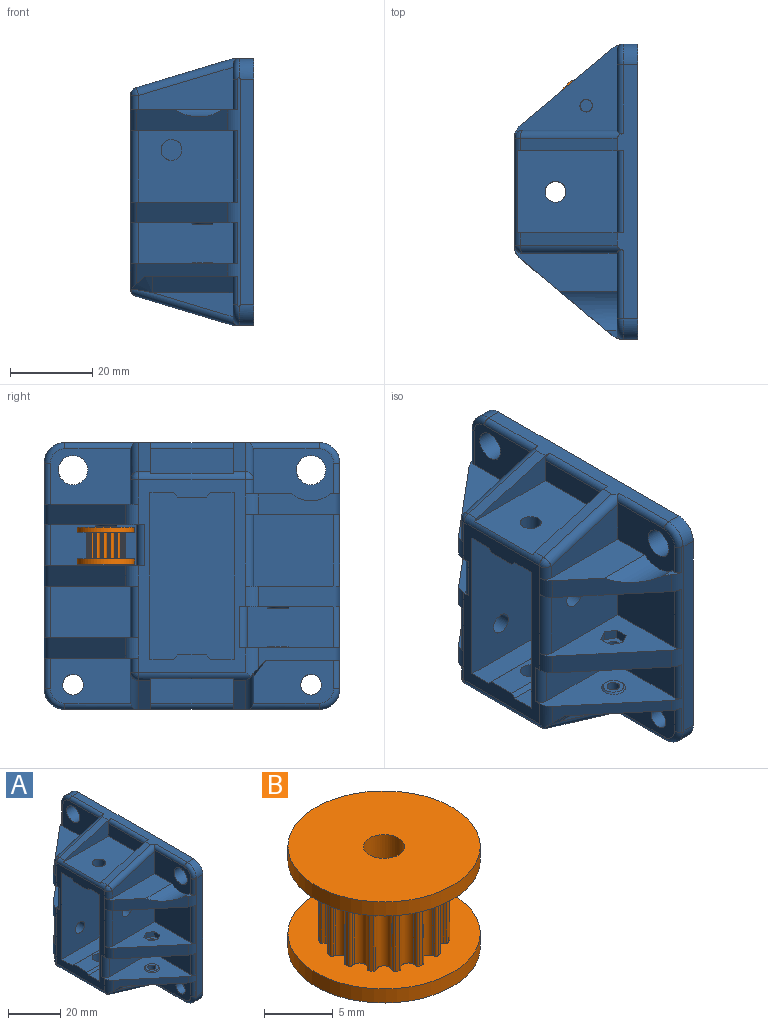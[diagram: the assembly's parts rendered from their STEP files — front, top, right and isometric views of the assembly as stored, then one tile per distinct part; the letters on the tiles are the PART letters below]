
ASSEMBLY  parts=2 mates=1
PART A: 149 faces, bbox 30.9x73.2x66.2 mm
  f0: cylinder r=1.55mm len=3.1mm, axis (0,0,1), area 30.2mm2, adj f78,f124
  f1: cylinder r=1.55mm len=3.1mm, axis (0,0,-1), area 30.2mm2, adj f81,f117
  f2: plane 3.79x2.2mm, normal (0,0,1), area 3.1mm2, adj f7,f71,f90,f108,f115
  f3: plane 25x11.25mm, normal (0,0,1), area 180.6mm2, adj f7,f19,f37,f71,f90,f132,f148
  f4: plane 20x6mm, normal (-1,0,0), area 120mm2, adj f5,f64,f65,f109
  f5: plane 24.34x20mm, normal (0,0,-1), area 466.3mm2, adj f4,f64,f65,f86,f136
  f6: plane 19.58x11mm, normal (-1,0,0), area 192.1mm2, adj f28,f41,f56,f94,f103,f104,f105
  f7: plane 19.58x12.7mm, normal (-1,0,0), area 183mm2, adj f2,f3,f26,f37,f90,f91,f106,f107
  f8: plane 24.34x20mm, normal (0,0,1), area 466.3mm2, adj f9,f62,f63,f87,f135
  f9: plane 20x6mm, normal (-1,0,0), area 120mm2, adj f8,f62,f63,f110
  f10: plane 21x10mm, normal (-1,0,0), area 210mm2, adj f34,f35,f36,f111
  f11: plane 21x10mm, normal (-1,0,0), area 210mm2, adj f38,f39,f40,f114
  f12: plane 19.5x17.5mm, normal (-1,0,0), area 341.3mm2, adj f13,f59,f61,f113
  f13: plane 23x17.5mm, normal (0,-1,0), area 382.1mm2, adj f12,f59,f61,f88,f139
  f14: plane 19.58x10.5mm, normal (-1,0,0), area 176.3mm2, adj f15,f29,f58,f93,f95,f100,f101,f102
  f15: plane 19.71x5.91mm, normal (0,-1,0), area 58.3mm2, adj f14,f93,f95
  f16: plane 19.58x13.5mm, normal (-1,0,0), area 220.7mm2, adj f18,f27,f55,f92,f97,f98,f99
  f17: plane 23x12.5mm, normal (0,1,0), area 267.1mm2, adj f20,f57,f60,f89,f140
  f18: plane 23x12.91mm, normal (0,1,0), area 217.6mm2, adj f16,f55,f92,f131
  f19: plane 47.02x26.27mm, normal (-1,0,0), area 382.6mm2, adj f3,f34,f36,f38,f40,f42,f43,f44
  f20: plane 19.5x12.5mm, normal (-1,0,0), area 243.8mm2, adj f17,f57,f60,f112
  f21: plane 55x3.18mm, normal (0,-1,0), area 174.8mm2, adj f25,f30,f33,f115
  f22: plane 62x5mm, normal (0,0,-1), area 228.5mm2, adj f25,f30,f31,f64,f65,f72,f73,f93
  f23: plane 55x3.18mm, normal (0,1,0), area 174.8mm2, adj f25,f31,f32,f116
  f24: plane 62x5mm, normal (0,0,1), area 228.5mm2, adj f25,f32,f33,f62,f63,f74,f75,f91
  f25: plane 72x65mm, normal (1,0,0), area 4539.1mm2, adj f21,f22,f23,f24,f26,f27,f28,f29
  f26: cylinder r=3.56mm len=7.13mm, axis (1,0,0), area 112mm2, adj f7,f25
  f27: cylinder r=3.56mm len=7.13mm, axis (1,0,0), area 112mm2, adj f16,f25
  f28: cylinder r=2.51mm len=5.02mm, axis (1,0,0), area 78.9mm2, adj f6,f25
  f29: cylinder r=2.51mm len=5.02mm, axis (1,0,0), area 78.9mm2, adj f14,f25
  f30: cylinder r=5mm len=5mm, axis (-1,0,0), area 27.4mm2, adj f21,f22,f25,f101,f115
  f31: cylinder r=5mm len=5mm, axis (1,0,0), area 27.4mm2, adj f22,f23,f25,f104,f116
  f32: cylinder r=5mm len=5mm, axis (-1,0,0), area 27.4mm2, adj f23,f24,f25,f98,f116
  f33: cylinder r=5mm len=5mm, axis (1,0,0), area 27.4mm2, adj f21,f24,f25,f107,f115
  f34: plane 26.12x24.45mm, normal (0,0,1), area 274.1mm2, adj f10,f19,f35,f69,f84,f111,f115,f142
  f35: plane 23x10mm, normal (0,-1,0), area 230mm2, adj f10,f34,f36,f142
  f36: plane 26.12x24.45mm, normal (0,0,-1), area 274.1mm2, adj f10,f19,f35,f70,f83,f111,f115,f142
  f37: plane 23x10.41mm, normal (0,-1,0), area 160.1mm2, adj f3,f7,f91,f132
  f38: plane 26.12x24.45mm, normal (0,0,-1), area 274.1mm2, adj f11,f19,f39,f66,f77,f114,f116,f141
  f39: plane 23x10mm, normal (0,1,0), area 230mm2, adj f11,f38,f40,f141
  f40: plane 26.12x24.45mm, normal (0,0,1), area 274.1mm2, adj f11,f19,f39,f67,f79,f114,f116,f141
  f41: plane 23x10.41mm, normal (0,1,0), area 160.1mm2, adj f6,f56,f94,f138
  f42: plane 40.5x25mm, normal (0,1,0), area 992.1mm2, adj f19,f43,f49,f50,f88
  f43: plane 25x5.75mm, normal (0,0,-1), area 143.8mm2, adj f19,f42,f50,f54
  f44: plane 25x7mm, normal (0,0,-1), area 154.6mm2, adj f19,f50,f53,f54,f87
  f45: plane 25x5.75mm, normal (0,0,-1), area 143.8mm2, adj f19,f46,f50,f53
  f46: plane 40.5x25mm, normal (0,-1,0), area 992.1mm2, adj f19,f45,f47,f50,f89
  f47: plane 25x5.75mm, normal (0,0,1), area 143.8mm2, adj f19,f46,f50,f51
  f48: plane 25x7mm, normal (0,0,1), area 154.6mm2, adj f19,f50,f51,f52,f86
  f49: plane 25x5.75mm, normal (0,0,1), area 143.8mm2, adj f19,f42,f50,f52
  f50: plane 40.5x20.5mm, normal (-1,0,0), area 814.3mm2, adj f42,f43,f44,f45,f46,f47,f48,f49
  f51: plane 25x1mm, normal (0,0.71,0.71), area 35.4mm2, adj f19,f47,f48,f50
  f52: plane 25x1mm, normal (0,-0.71,0.71), area 35.4mm2, adj f19,f48,f49,f50
  f53: plane 25x1mm, normal (0,0.71,-0.71), area 35.4mm2, adj f19,f44,f45,f50
  f54: plane 25x1mm, normal (0,-0.71,-0.71), area 35.4mm2, adj f19,f43,f44,f50
  f55: plane 26.12x22.95mm, normal (0,0,1), area 255.4mm2, adj f16,f18,f19,f66,f80,f99,f116,f131
  f56: plane 26.12x22.95mm, normal (0,0,-1), area 263mm2, adj f6,f19,f41,f68,f105,f116,f138,f145
  f57: plane 26.12x22.95mm, normal (0,0,1), area 263mm2, adj f17,f19,f20,f68,f112,f116,f140,f145
  f58: plane 22.58x17.98mm, normal (0,0,-1), area 185.4mm2, adj f14,f69,f85,f95,f96,f100,f115
  f59: plane 26.12x22.95mm, normal (0,0,-1), area 263mm2, adj f12,f13,f19,f71,f113,f115,f139,f148
  f60: plane 26.12x22.95mm, normal (0,0,-1), area 236.8mm2, adj f17,f19,f20,f67,f112,f116,f125,f126
  f61: plane 26.12x22.95mm, normal (0,0,1), area 236.8mm2, adj f12,f13,f19,f70,f113,f115,f118,f119
  f62: plane 25.84x7.5mm, normal (0,-1,0), area 94.1mm2, adj f8,f9,f24,f74,f110,f135
  f63: plane 25.84x7.5mm, normal (0,1,0), area 94.1mm2, adj f8,f9,f24,f75,f110,f135
  f64: plane 25.84x7.5mm, normal (0,-1,0), area 94.1mm2, adj f4,f5,f22,f72,f109,f136
  f65: plane 25.84x7.5mm, normal (0,1,0), area 94.1mm2, adj f4,f5,f22,f73,f109,f136
  f66: plane 22.18x18.63mm, normal (-0.64,0.77,0), area 144.8mm2, adj f38,f55,f116,f143
  f67: plane 22.18x18.63mm, normal (-0.64,0.77,0), area 144.8mm2, adj f40,f60,f116,f144
  f68: plane 22.18x18.63mm, normal (-0.64,0.77,0), area 144.8mm2, adj f56,f57,f116,f145
  f69: plane 22.27x18.72mm, normal (-0.64,-0.77,0), area 89.6mm2, adj f34,f58,f96,f115,f146
  f70: plane 22.18x18.63mm, normal (-0.64,-0.77,0), area 144.8mm2, adj f36,f61,f115,f147
  f71: plane 22.54x18.99mm, normal (-0.64,-0.77,0), area 127.6mm2, adj f2,f3,f59,f90,f115,f148
  f72: plane 23.57x7.07mm, normal (-0.29,0,-0.96), area 73.8mm2, adj f22,f64,f94,f136
  f73: plane 23.57x7.07mm, normal (-0.29,0,-0.96), area 73.8mm2, adj f22,f65,f93,f136
  f74: plane 23.57x7.07mm, normal (-0.29,0,0.96), area 73.8mm2, adj f24,f62,f92,f135
  f75: plane 23.57x7.07mm, normal (-0.29,0,0.96), area 73.8mm2, adj f24,f63,f91,f135
  f76: plane 5x5mm, normal (0,0,-1), area 12.1mm2, adj f77,f80
  f77: cone r=2.5mm half-angle=45deg, axis (0,0,1), area 9.6mm2, adj f38,f76
  f78: plane 5x5mm, normal (0,0,1), area 12.1mm2, adj f0,f79
  f79: cone r=2.5mm half-angle=45deg, axis (0,0,-1), area 9.6mm2, adj f40,f78
  f80: cylinder r=1.55mm len=5.4mm, axis (0,0,1), area 52.6mm2, adj f55,f76
  f81: plane 5x5mm, normal (0,0,-1), area 12.1mm2, adj f1,f83
  f82: plane 5x5mm, normal (0,0,1), area 12.1mm2, adj f84,f85
  f83: cone r=2.5mm half-angle=45deg, axis (0,0,1), area 9.6mm2, adj f36,f81
  f84: cone r=2.5mm half-angle=45deg, axis (0,0,-1), area 9.6mm2, adj f34,f82
  f85: cylinder r=1.55mm len=3.4mm, axis (0,0,-1), area 33.1mm2, adj f58,f82
  f86: cylinder r=2.55mm len=5.75mm, axis (0,0,1), area 92.1mm2, adj f5,f48
  f87: cylinder r=2.55mm len=5.75mm, axis (0,0,1), area 92.1mm2, adj f8,f44
  f88: cylinder r=2.55mm len=5.1mm, axis (0,-1,0), area 76.1mm2, adj f13,f42
  f89: cylinder r=2.55mm len=5.1mm, axis (0,1,0), area 76.1mm2, adj f17,f46
  f90: cylinder r=7.5mm len=13.99mm, axis (1,0,0), area 85.8mm2, adj f2,f3,f7,f71
  f91: cylinder r=2mm len=25.53mm, axis (-0.96,0,-0.29), area 77.5mm2, adj f7,f24,f37,f75,f106,f134
  f92: cylinder r=2mm len=25.53mm, axis (0.96,0,0.29), area 77.5mm2, adj f16,f18,f24,f74,f97,f133
  f93: cylinder r=2mm len=26.94mm, axis (-0.96,0,0.29), area 79.5mm2, adj f14,f15,f22,f73,f96,f102,f136,f146
  f94: cylinder r=2mm len=25.53mm, axis (0.96,0,-0.29), area 77.5mm2, adj f6,f22,f41,f72,f103,f137
  f95: plane 19.71x4mm, normal (0,-0.8,-0.6), area 98.5mm2, adj f14,f15,f58,f96
  f96: bspline ~5.84x4mm, area 16.6mm2, adj f58,f69,f93,f95,f146
  f97: cylinder r=1.5mm len=16.76mm, axis (0,-1,0), area 38.7mm2, adj f16,f24,f92,f98
  f98: torus R=3.5mm, axis (1,0,0), area 16.4mm2, adj f16,f32,f97,f99,f116
  f99: cylinder r=1.5mm len=10mm, axis (0,0,1), area 19.7mm2, adj f16,f55,f98,f116
  f100: cylinder r=1.5mm len=7mm, axis (0,0,-1), area 13.8mm2, adj f14,f58,f101,f115
  f101: torus R=3.5mm, axis (1,0,0), area 16.4mm2, adj f14,f30,f100,f102,f115
  f102: cylinder r=1.5mm len=16.76mm, axis (0,1,0), area 38.7mm2, adj f14,f22,f93,f101
  f103: cylinder r=1.5mm len=16.76mm, axis (0,1,0), area 38.7mm2, adj f6,f22,f94,f104
  f104: torus R=3.5mm, axis (1,0,0), area 16.4mm2, adj f6,f31,f103,f105,f116
  f105: cylinder r=1.5mm len=7.5mm, axis (0,0,1), area 14.8mm2, adj f6,f56,f104,f116
  f106: cylinder r=1.5mm len=16.76mm, axis (0,-1,0), area 38.7mm2, adj f7,f24,f91,f107
  f107: torus R=3.5mm, axis (1,0,0), area 16.4mm2, adj f7,f33,f106,f108,f115
  f108: cylinder r=1.5mm len=7.5mm, axis (0,0,-1), area 14.8mm2, adj f2,f7,f107,f115
  f109: cylinder r=1.5mm len=20mm, axis (0,1,0), area 47.1mm2, adj f4,f22,f64,f65
  f110: cylinder r=1.5mm len=20mm, axis (0,-1,0), area 47.1mm2, adj f9,f24,f62,f63
  f111: cylinder r=1.5mm len=10mm, axis (0,0,-1), area 19.7mm2, adj f10,f34,f36,f115
  f112: cylinder r=1.5mm len=12.5mm, axis (0,0,1), area 24.6mm2, adj f20,f57,f60,f116
  f113: cylinder r=1.5mm len=17.5mm, axis (0,0,-1), area 34.4mm2, adj f12,f59,f61,f115
  f114: cylinder r=1.5mm len=10mm, axis (0,0,1), area 19.7mm2, adj f11,f38,f40,f116
  f115: cylinder r=5mm len=55.64mm, axis (0,0,1), area 75.4mm2, adj f2,f21,f30,f33,f34,f36,f58,f59
  f116: cylinder r=5mm len=55.64mm, axis (0,0,-1), area 80.9mm2, adj f23,f31,f32,f38,f40,f55,f56,f57
  f117: plane 6.35x5.5mm, normal (0,0,1), area 18.6mm2, adj f1,f118,f119,f120,f121,f122,f123
  f118: plane 2.75x2.3mm, normal (0.5,0.87,0), area 7.3mm2, adj f61,f117,f119,f123
  f119: plane 2.75x2.3mm, normal (-0.5,0.87,0), area 7.3mm2, adj f61,f117,f118,f120
  f120: plane 3.18x2.3mm, normal (-1,0,0), area 7.3mm2, adj f61,f117,f119,f121
  f121: plane 2.75x2.3mm, normal (-0.5,-0.87,0), area 7.3mm2, adj f61,f117,f120,f122
  f122: plane 2.75x2.3mm, normal (0.5,-0.87,0), area 7.3mm2, adj f61,f117,f121,f123
  f123: plane 3.18x2.3mm, normal (1,0,0), area 7.3mm2, adj f61,f117,f118,f122
  f124: plane 6.35x5.5mm, normal (0,0,-1), area 18.6mm2, adj f0,f125,f126,f127,f128,f129,f130
  f125: plane 2.75x2.3mm, normal (0.5,-0.87,0), area 7.3mm2, adj f60,f124,f126,f130
  f126: plane 2.75x2.3mm, normal (-0.5,-0.87,0), area 7.3mm2, adj f60,f124,f125,f127
  f127: plane 3.18x2.3mm, normal (-1,0,0), area 7.3mm2, adj f60,f124,f126,f128
  f128: plane 2.75x2.3mm, normal (-0.5,0.87,0), area 7.3mm2, adj f60,f124,f127,f129
  f129: plane 2.75x2.3mm, normal (0.5,0.87,0), area 7.3mm2, adj f60,f124,f128,f130
  f130: plane 3.18x2.3mm, normal (1,0,0), area 7.3mm2, adj f60,f124,f125,f129
  f131: cylinder r=2mm len=6.01mm, axis (0,0,1), area 18.9mm2, adj f18,f19,f55,f133
  f132: cylinder r=2mm len=3.51mm, axis (0,0,-1), area 11mm2, adj f3,f19,f37,f134
  f133: sphere r=2mm, area 5.4mm2, adj f92,f131,f135
  f134: sphere r=2mm, area 5.1mm2, adj f91,f132,f135
  f135: cylinder r=2mm len=26mm, axis (0,-1,0), area 48.9mm2, adj f8,f19,f62,f63,f74,f75,f133,f134
  f136: cylinder r=2mm len=27.44mm, axis (0,-1,0), area 50.8mm2, adj f5,f19,f64,f65,f72,f73,f93,f137
  f137: sphere r=2mm, area 5.4mm2, adj f94,f136,f138
  f138: cylinder r=2mm len=3.51mm, axis (0,0,1), area 11mm2, adj f19,f41,f56,f137
  f139: cylinder r=2mm len=17.5mm, axis (0,0,-1), area 55mm2, adj f13,f19,f59,f61
  f140: cylinder r=2mm len=12.5mm, axis (0,0,1), area 39.3mm2, adj f17,f19,f57,f60
  f141: cylinder r=2mm len=10mm, axis (0,0,1), area 31.4mm2, adj f19,f38,f39,f40
  f142: cylinder r=2mm len=10mm, axis (0,0,-1), area 31.4mm2, adj f19,f34,f35,f36
  f143: cylinder r=4mm len=5mm, axis (0,0,1), area 17.4mm2, adj f19,f38,f55,f66
  f144: cylinder r=4mm len=5mm, axis (0,0,1), area 17.4mm2, adj f19,f40,f60,f67
  f145: cylinder r=4mm len=5mm, axis (0,0,1), area 17.4mm2, adj f19,f56,f57,f68
  f146: cylinder r=4mm len=6.92mm, axis (0,0,1), area 21.1mm2, adj f19,f34,f69,f93,f96,f136
  f147: cylinder r=4mm len=5mm, axis (0,0,1), area 17.4mm2, adj f19,f36,f61,f70
  f148: cylinder r=4mm len=5mm, axis (0,0,1), area 17.4mm2, adj f3,f19,f59,f71
PART B: 105 faces, bbox 14x14x9 mm
  f0: cylinder r=7mm len=14mm, axis (0,0,-1), area 55mm2, adj f1,f2
  f1: plane 14x14mm, normal (0,0,1), area 91.5mm2, adj f0,f3,f4,f5,f6,f7,f8,f9
  f2: plane 14x14mm, normal (0,0,-1), area 146.9mm2, adj f0,f104
  f3: plane 1.6x0.77mm, normal (0,0,1), area 0.7mm2, adj f1,f31,f32,f33,f34,f35
  f4: plane 0.29x0.06mm, normal (0,0,1), area 0mm2, adj f1,f36
  f5: cylinder r=0.19mm len=6.5mm, axis (0,0,1), area 1.7mm2, adj f1,f6,f100,f103
  f6: plane 6.5x0.29mm, normal (-0.2,0.98,0), area 1.9mm2, adj f1,f5,f7,f103
  f7: cylinder r=0.19mm len=6.5mm, axis (0,0,1), area 1.7mm2, adj f1,f6,f8,f103
  f8: cylinder r=5.01mm len=6.5mm, axis (0,0,1), area 1.5mm2, adj f1,f7,f9,f103
  f9: cylinder r=0.56mm len=6.5mm, axis (0,0,1), area 8.7mm2, adj f1,f8,f10,f103
  f10: cylinder r=5.01mm len=6.5mm, axis (0,0,1), area 1.5mm2, adj f1,f9,f11,f103
  f11: cylinder r=0.19mm len=6.5mm, axis (0,0,1), area 1.7mm2, adj f1,f10,f12,f103
  f12: plane 6.5x0.29mm, normal (0.2,0.98,0), area 1.9mm2, adj f1,f11,f13,f103
  f13: cylinder r=0.19mm len=6.5mm, axis (0,0,1), area 1.7mm2, adj f1,f12,f14,f103
  f14: cylinder r=5.01mm len=6.5mm, axis (0,0,1), area 1.5mm2, adj f1,f13,f15,f103
  f15: cylinder r=0.56mm len=6.5mm, axis (0,0,1), area 8.7mm2, adj f1,f14,f16,f103
  f16: cylinder r=5.01mm len=6.5mm, axis (0,0,1), area 1.5mm2, adj f1,f15,f17,f103
  f17: cylinder r=0.19mm len=6.5mm, axis (0,0,1), area 1.7mm2, adj f1,f16,f18,f103
  f18: plane 6.5x0.25mm, normal (0.56,0.83,0), area 1.9mm2, adj f1,f17,f19,f103
  f19: cylinder r=0.19mm len=6.5mm, axis (0,0,1), area 1.7mm2, adj f1,f18,f20,f103
  f20: cylinder r=5.01mm len=6.5mm, axis (0,0,1), area 1.5mm2, adj f1,f19,f21,f103
  f21: cylinder r=0.56mm len=6.5mm, axis (0,0,1), area 8.7mm2, adj f1,f20,f22,f103
  f22: cylinder r=5.01mm len=6.5mm, axis (0,0,1), area 1.5mm2, adj f1,f21,f23,f103
  f23: cylinder r=0.19mm len=6.5mm, axis (0,0,1), area 1.7mm2, adj f1,f22,f24,f103
  f24: plane 6.5x0.25mm, normal (0.83,0.56,0), area 1.9mm2, adj f1,f23,f25,f103
  f25: cylinder r=0.19mm len=6.5mm, axis (0,0,1), area 1.7mm2, adj f1,f24,f26,f103
  f26: cylinder r=5.01mm len=6.5mm, axis (0,0,1), area 1.5mm2, adj f1,f25,f27,f103
  f27: cylinder r=0.56mm len=6.5mm, axis (0,0,1), area 8.7mm2, adj f1,f26,f28,f103
  f28: cylinder r=5.01mm len=6.5mm, axis (0,0,1), area 1.5mm2, adj f1,f27,f29,f103
  f29: cylinder r=0.19mm len=6.5mm, axis (0,0,1), area 1.7mm2, adj f1,f28,f30,f103
  f30: plane 6.5x0.29mm, normal (0.98,0.2,0), area 1.9mm2, adj f1,f29,f31,f103
  f31: cylinder r=0.19mm len=6.5mm, axis (0,0,1), area 1.7mm2, adj f3,f30,f32,f103
  f32: cylinder r=5.01mm len=6.5mm, axis (0,0,1), area 1.5mm2, adj f3,f31,f33,f103
  f33: cylinder r=0.56mm len=6.5mm, axis (0,0,1), area 8.7mm2, adj f3,f32,f34,f103
  f34: cylinder r=5.01mm len=6.5mm, axis (0,0,1), area 1.5mm2, adj f3,f33,f35,f103
  f35: cylinder r=0.19mm len=6.5mm, axis (0,0,1), area 1.7mm2, adj f3,f34,f36,f103
  f36: plane 6.5x0.29mm, normal (0.98,-0.2,0), area 1.9mm2, adj f4,f35,f37,f103
  f37: cylinder r=0.19mm len=6.5mm, axis (0,0,1), area 1.7mm2, adj f1,f36,f38,f103
  f38: cylinder r=5.01mm len=6.5mm, axis (0,0,1), area 1.5mm2, adj f1,f37,f39,f103
  f39: cylinder r=0.56mm len=6.5mm, axis (0,0,1), area 8.7mm2, adj f1,f38,f40,f103
  f40: cylinder r=5.01mm len=6.5mm, axis (0,0,1), area 1.5mm2, adj f1,f39,f41,f103
  f41: cylinder r=0.19mm len=6.5mm, axis (0,0,1), area 1.7mm2, adj f1,f40,f42,f103
  f42: plane 6.5x0.25mm, normal (0.83,-0.56,0), area 1.9mm2, adj f1,f41,f43,f103
  f43: cylinder r=0.19mm len=6.5mm, axis (0,0,1), area 1.7mm2, adj f1,f42,f44,f103
  f44: cylinder r=5.01mm len=6.5mm, axis (0,0,1), area 1.5mm2, adj f1,f43,f45,f103
  f45: cylinder r=0.56mm len=6.5mm, axis (0,0,1), area 8.7mm2, adj f1,f44,f46,f103
  f46: cylinder r=5.01mm len=6.5mm, axis (0,0,1), area 1.5mm2, adj f1,f45,f47,f103
  f47: cylinder r=0.19mm len=6.5mm, axis (0,0,1), area 1.7mm2, adj f1,f46,f48,f103
  f48: plane 6.5x0.25mm, normal (0.56,-0.83,0), area 1.9mm2, adj f1,f47,f49,f103
  f49: cylinder r=0.19mm len=6.5mm, axis (0,0,1), area 1.7mm2, adj f1,f48,f50,f103
  f50: cylinder r=5.01mm len=6.5mm, axis (0,0,1), area 1.5mm2, adj f1,f49,f51,f103
  f51: cylinder r=0.56mm len=6.5mm, axis (0,0,1), area 8.7mm2, adj f1,f50,f52,f103
  f52: cylinder r=5.01mm len=6.5mm, axis (0,0,1), area 1.5mm2, adj f1,f51,f53,f103
  f53: cylinder r=0.19mm len=6.5mm, axis (0,0,1), area 1.7mm2, adj f1,f52,f54,f103
  f54: plane 6.5x0.29mm, normal (0.2,-0.98,0), area 1.9mm2, adj f1,f53,f55,f103
  f55: cylinder r=0.19mm len=6.5mm, axis (0,0,1), area 1.7mm2, adj f1,f54,f56,f103
  f56: cylinder r=5.01mm len=6.5mm, axis (0,0,1), area 1.5mm2, adj f1,f55,f57,f103
  f57: cylinder r=0.56mm len=6.5mm, axis (0,0,1), area 8.7mm2, adj f1,f56,f58,f103
  f58: cylinder r=5.01mm len=6.5mm, axis (0,0,1), area 1.5mm2, adj f1,f57,f59,f103
  f59: cylinder r=0.19mm len=6.5mm, axis (0,0,1), area 1.7mm2, adj f1,f58,f60,f103
  f60: plane 6.5x0.29mm, normal (-0.2,-0.98,0), area 1.9mm2, adj f1,f59,f61,f103
  f61: cylinder r=0.19mm len=6.5mm, axis (0,0,1), area 1.7mm2, adj f1,f60,f62,f103
  f62: cylinder r=5.01mm len=6.5mm, axis (0,0,1), area 1.5mm2, adj f1,f61,f63,f103
  f63: cylinder r=0.56mm len=6.5mm, axis (0,0,1), area 8.7mm2, adj f1,f62,f64,f103
  f64: cylinder r=5.01mm len=6.5mm, axis (0,0,1), area 1.5mm2, adj f1,f63,f65,f103
  f65: cylinder r=0.19mm len=6.5mm, axis (0,0,1), area 1.7mm2, adj f1,f64,f66,f103
  f66: plane 6.5x0.25mm, normal (-0.56,-0.83,0), area 1.9mm2, adj f1,f65,f67,f103
  f67: cylinder r=0.19mm len=6.5mm, axis (0,0,1), area 1.7mm2, adj f1,f66,f68,f103
  f68: cylinder r=5.01mm len=6.5mm, axis (0,0,1), area 1.5mm2, adj f1,f67,f69,f103
  f69: cylinder r=0.56mm len=6.5mm, axis (0,0,1), area 8.7mm2, adj f1,f68,f70,f103
  f70: cylinder r=5.01mm len=6.5mm, axis (0,0,1), area 1.5mm2, adj f1,f69,f71,f103
  f71: cylinder r=0.19mm len=6.5mm, axis (0,0,1), area 1.7mm2, adj f1,f70,f72,f103
  f72: plane 6.5x0.25mm, normal (-0.83,-0.56,0), area 1.9mm2, adj f1,f71,f73,f103
  f73: cylinder r=0.19mm len=6.5mm, axis (0,0,1), area 1.7mm2, adj f1,f72,f74,f103
  f74: cylinder r=5.01mm len=6.5mm, axis (0,0,1), area 1.5mm2, adj f1,f73,f75,f103
  f75: cylinder r=0.56mm len=6.5mm, axis (0,0,1), area 8.7mm2, adj f1,f74,f76,f103
  f76: cylinder r=5.01mm len=6.5mm, axis (0,0,1), area 1.5mm2, adj f1,f75,f77,f103
  f77: cylinder r=0.19mm len=6.5mm, axis (0,0,1), area 1.7mm2, adj f1,f76,f78,f103
  f78: plane 6.5x0.29mm, normal (-0.98,-0.2,0), area 1.9mm2, adj f1,f77,f79,f103
  f79: cylinder r=0.19mm len=6.5mm, axis (0,0,1), area 1.7mm2, adj f1,f78,f80,f103
  f80: cylinder r=5.01mm len=6.5mm, axis (0,0,1), area 1.5mm2, adj f1,f79,f81,f103
  f81: cylinder r=0.56mm len=6.5mm, axis (0,0,1), area 8.7mm2, adj f1,f80,f82,f103
  f82: cylinder r=5.01mm len=6.5mm, axis (0,0,1), area 1.5mm2, adj f1,f81,f83,f103
  f83: cylinder r=0.19mm len=6.5mm, axis (0,0,1), area 1.7mm2, adj f1,f82,f84,f103
  f84: plane 6.5x0.29mm, normal (-0.98,0.2,0), area 1.9mm2, adj f1,f83,f85,f103
  f85: cylinder r=0.19mm len=6.5mm, axis (0,0,1), area 1.7mm2, adj f1,f84,f86,f103
  f86: cylinder r=5.01mm len=6.5mm, axis (0,0,1), area 1.5mm2, adj f1,f85,f87,f103
  f87: cylinder r=0.56mm len=6.5mm, axis (0,0,1), area 8.7mm2, adj f1,f86,f88,f103
  f88: cylinder r=5.01mm len=6.5mm, axis (0,0,1), area 1.5mm2, adj f1,f87,f89,f103
  f89: cylinder r=0.19mm len=6.5mm, axis (0,0,1), area 1.7mm2, adj f1,f88,f90,f103
  f90: plane 6.5x0.25mm, normal (-0.83,0.56,0), area 1.9mm2, adj f1,f89,f91,f103
  f91: cylinder r=0.19mm len=6.5mm, axis (0,0,1), area 1.7mm2, adj f1,f90,f92,f103
  f92: cylinder r=5.01mm len=6.5mm, axis (0,0,1), area 1.5mm2, adj f1,f91,f93,f103
  f93: cylinder r=0.56mm len=6.5mm, axis (0,0,1), area 8.7mm2, adj f1,f92,f94,f103
  f94: cylinder r=5.01mm len=6.5mm, axis (0,0,1), area 1.5mm2, adj f1,f93,f95,f103
  f95: cylinder r=0.19mm len=6.5mm, axis (0,0,1), area 1.7mm2, adj f1,f94,f96,f103
  f96: plane 6.5x0.25mm, normal (-0.56,0.83,0), area 1.9mm2, adj f1,f95,f97,f103
  f97: cylinder r=0.19mm len=6.5mm, axis (0,0,1), area 1.7mm2, adj f1,f96,f98,f103
  f98: cylinder r=5.01mm len=6.5mm, axis (0,0,1), area 1.5mm2, adj f1,f97,f99,f103
  f99: cylinder r=0.56mm len=6.5mm, axis (0,0,1), area 8.7mm2, adj f1,f98,f100,f103
  f100: cylinder r=5.01mm len=6.5mm, axis (0,0,1), area 1.5mm2, adj f1,f5,f99,f103
  f101: cylinder r=7mm len=14mm, axis (0,0,-1), area 55mm2, adj f102,f103
  f102: plane 14x14mm, normal (0,0,1), area 146.9mm2, adj f101,f104
  f103: plane 14x14mm, normal (0,0,-1), area 92.3mm2, adj f5,f6,f7,f8,f9,f10,f11,f12
  f104: cylinder r=1.5mm len=9mm, axis (0,0,1), area 84.8mm2, adj f2,f102
PLACE A t=(4.56,-14.33,4.87)mm
PLACE B t=(-27.94,6.67,7.77)mm
MATE fastened B.f0 <-> A.f0  axis (0,0,-1) through (-27.94,6.67,7.77)mm
